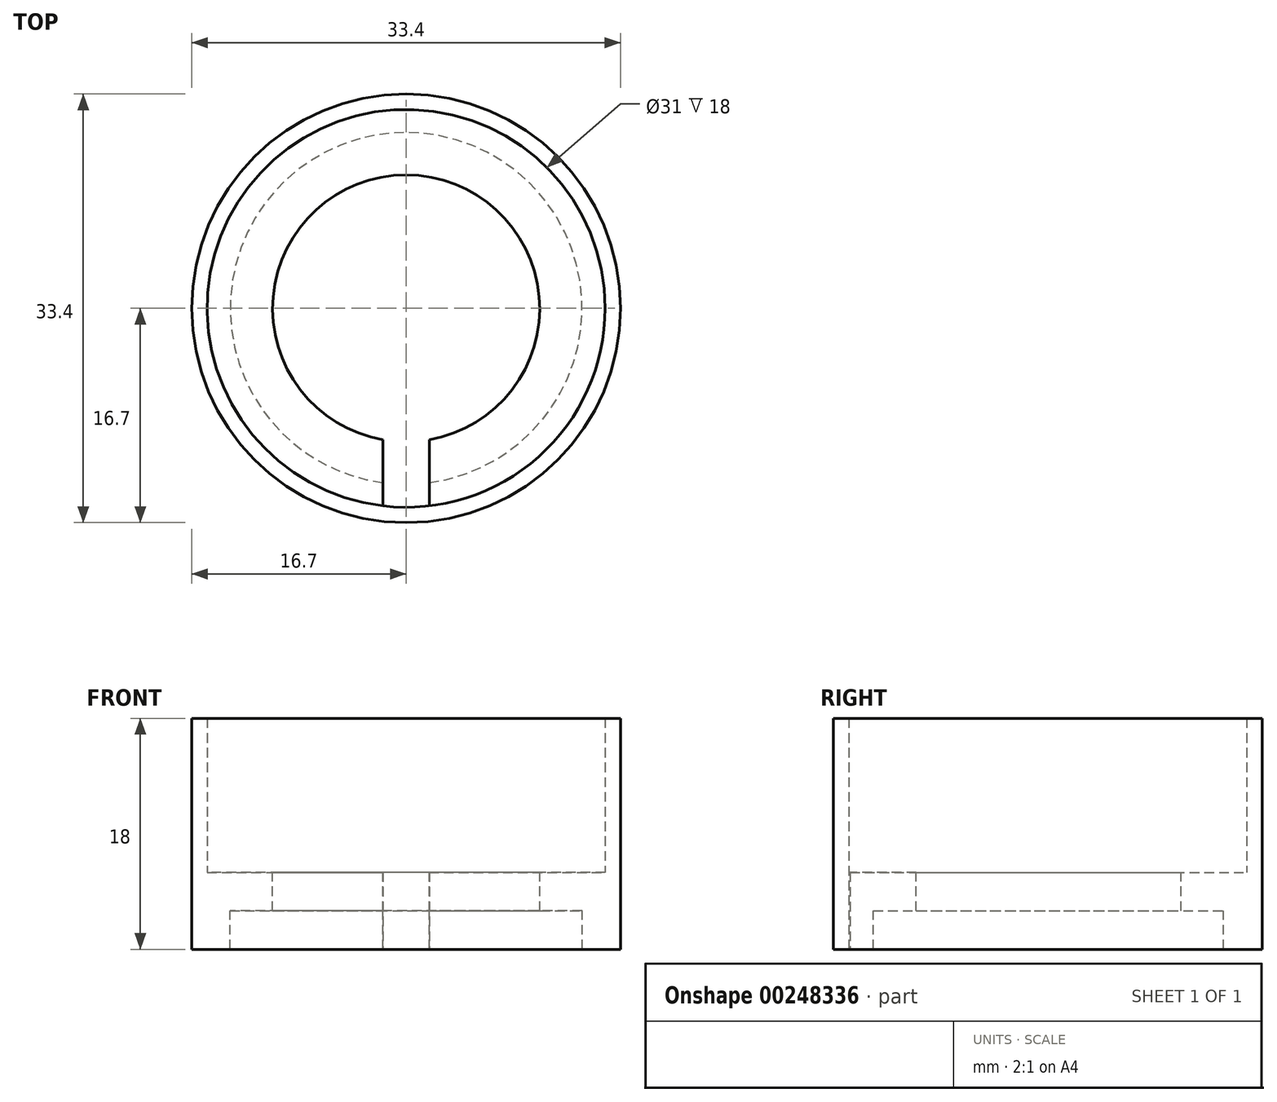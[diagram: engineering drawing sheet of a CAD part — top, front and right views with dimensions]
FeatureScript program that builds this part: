
annotation { "Feature Type Name" : "Feature", "Feature Type Description" : "" }
export const myFeature = defineFeature(function(context is Context, id is Id, definition is map)
    precondition{}
    {
        {
            var Q0;
            Q0=qCreatedBy(makeId("Top.planeOp"),FACE);
            var sketch = newSketch(context, id + "F0", { "sketchPlane" : qUnion([Q0])});
            skCircle(sketch, "E0", {"center": v(0, 0) * mm, "radius": 15.5 * mm});
            skCircle(sketch, "E1", {"center": v(0, 0) * mm, "radius": 16.7 * mm});
            skSolve(sketch);
        }
        {
            var Q0;
            Q0 = qSketchRegion(id + "F0", true);
            extrude(context, id + "F1", {"entities" : qUnion([Q0]), "depth" : 15 * mm});
        }
        {
            var Q0;
            Q0=makeQuery(id+"F1.opExtrude","CAP_FACE",FACE,{"disambiguationData":[OSD([sQuery(id+"F0.wireOp",EDGE,"E0"),sQuery(id+"F0.wireOp",EDGE,"E1")])],"isStart":true});
            var sketch = newSketch(context, id + "F2", { "sketchPlane" : qUnion([Q0])});
            skCircle(sketch, "E2", {"center": v(0, 0) * mm, "radius": 15.5 * mm});
            skSolve(sketch);
        }
        {
            var Q0;
            Q0 = qSketchRegion(id + "F2", true);
            extrude(context, id + "F3", {"entities" : qUnion([Q0]), "operationType" : NewBodyOperationType.ADD, "oppositeDirection" : true, "depth" : 3 * mm});
        }
        {
            var Q0;
            Q0=makeQuery(id+"F3.opExtrude","CAP_FACE",FACE,{"disambiguationData":[OSD([sQuery(id+"F2.wireOp",EDGE,"E2")])],"isStart":false});
            var sketch = newSketch(context, id + "F4", { "sketchPlane" : qUnion([Q0])});
            skCircle(sketch, "E3", {"center": v(0, 0) * mm, "radius": 10.4 * mm});
            skSolve(sketch);
        }
        {
            var Q0;
            Q0 = qSketchRegion(id + "F4", true);
            extrude(context, id + "F5", {"entities" : qUnion([Q0]), "operationType" : NewBodyOperationType.REMOVE, "oppositeDirection" : true, "depth" : 25 * mm});
        }
        {
            var Q0;
            Q0=makeQuery(id+"F3.boolean.opBoolean","MERGE",FACE,{"derivedFrom":[makeQuery(id+"F1.opExtrude","CAP_FACE",FACE,{"disambiguationData":[OSD([sQuery(id+"F0.wireOp",EDGE,"E0"),sQuery(id+"F0.wireOp",EDGE,"E1")])],"isStart":true}),makeQuery(id+"F3.opExtrude","CAP_FACE",FACE,{"disambiguationData":[OSD([sQuery(id+"F2.wireOp",EDGE,"E2")])],"isStart":true})]});
            var sketch = newSketch(context, id + "F6", { "sketchPlane" : qUnion([Q0])});
            skCircle(sketch, "E4", {"center": v(0, 0) * mm, "radius": 16.7 * mm});
            skCircle(sketch, "E5", {"center": v(0, 0) * mm, "radius": 13.7 * mm});
            skSolve(sketch);
        }
        {
            var Q0;
            Q0 = qSketchRegion(id + "F6", true);
            extrude(context, id + "F7", {"entities" : qUnion([Q0]), "operationType" : NewBodyOperationType.ADD, "depth" : 3 * mm});
        }
        {
            var Q0;
            Q0=makeQuery(id+"F7.opExtrude","CAP_FACE",FACE,{"disambiguationData":[OSD([sQuery(id+"F6.wireOp",EDGE,"E4"),sQuery(id+"F6.wireOp",EDGE,"E5")])],"isStart":false});
            var sketch = newSketch(context, id + "F8", { "sketchPlane" : qUnion([Q0])});
            skSolve(sketch);
        }
        {
            var Q0;
            Q0=makeQuery(id+"F8.imprint","IMPRINT",FACE,{"disambiguationData":[TD([[makeQuery(id+"F8.imprint","IMPRINT",EDGE,{"derivedFrom":makeQuery(id+"F7.opExtrude","CAP_EDGE",EDGE,{"disambiguationData":[OSD([sQuery(id+"F6.wireOp",EDGE,"E4")])],"isStart":false})}),-1.0]])]});
            var sketch = newSketch(context, id + "F9", { "sketchPlane" : qUnion([Q0])});
            skLineSegment(sketch, "E6.bottom", {"start": v(1.8, 8.94) * mm, "end": v(-1.8, 8.94) * mm});
            skLineSegment(sketch, "E6.top", {"start": v(1.8, 17.74) * mm, "end": v(-1.8, 17.74) * mm});
            skLineSegment(sketch, "E6.left", {"start": v(1.8, 8.94) * mm, "end": v(1.8, 17.74) * mm});
            skLineSegment(sketch, "E6.right", {"start": v(-1.8, 8.94) * mm, "end": v(-1.8, 17.74) * mm});
            skPoint(sketch, "E6.middle", {"position": v(0, 13.34) * mm});
            skCircle(sketch, "E7", {"center": v(0, 0) * mm, "radius": 15.5 * mm});
            skSolve(sketch);
        }
        {
            var Q0;
            {var subQ0=sQuery(id+"F9.wireOp",EDGE,"E6.bottom");Q0=makeQuery(id+"F9.imprint","IMPRINT",FACE,{"disambiguationData":[TD([[makeQuery(id+"F9.imprint","IMPRINT",EDGE,{"derivedFrom":subQ0}),-1.0]])]});}
            var Q1;
            {var subQ0=sQuery(id+"F9.wireOp",EDGE,"E7");var subQ1=sQuery(id+"F9.wireOp",EDGE,"E6.left");var subQ2=makeQuery(id+"F9.imprint","INTERSECT",VERTEX,{"derivedFrom":[subQ1,subQ0]});Q1=makeQuery(id+"F9.imprint","IMPRINT",FACE,{"disambiguationData":[TD([[makeQuery(id+"F9.imprint","IMPRINT",EDGE,{"disambiguationData":[TD([[subQ2,1.0]])],"derivedFrom":subQ1}),1.0]])]});}
            extrude(context, id + "F10", {"entities" : qUnion([Q0, Q1]), "operationType" : NewBodyOperationType.REMOVE, "oppositeDirection" : true, "depth" : 25 * mm});
        }
    });
